# Revit family: 265-91-001 DN700-800
name_source: partatom
category: Pipe Accessories
units: mm (PartAtom-declared; Revit-internal decimal feet)

## family parameters
Always vertical = Yes
Cut with Voids When Loaded = No
Part Type = Valve - Breaks Into
Round Connector Dimension = Use Diameter
Shared = No
Work Plane-Based = No

## types (4) — shared parameters
25 = 25 mm  [stored 0.082021 ft]
Bolt.no = 24 mm  [stored 0.0787402 ft]
DN700_PN10 = 265-9-0700-11-04036401
DN700_PN16 = 265-9-0700-10-14036400
DN800_PN10 = 265-9-0800-11-04036401
DN800_PN16 = 265-9-0800-10-14036400
Description_ = AVK DISMANTLING JOINT WITH CENTRE FLANGE, PN10/16
Raised_dis = 5 mm  [stored 0.0164042 ft]
Search_table = 265-91-001 DN700-800
URL_product_pages = https://www.avkvalves.com
zero-valued in all types: Default Elevation

## per-type parameters (varying)
| type | B1 | Bore | D | DN | FL_T | FL_T/2 | L | L1 | L11 | L2 | L3 | Nut_T | PCD | PN | S | S11 | T | T1 | offset | raised_R |
| DN700_PN16 | 41 mm | 350 mm | 455 mm | 700 mm | 40 mm  [stored 0.131234 ft] | 20 mm  [stored 0.0656168 ft] | 515 mm | 204 mm | 300 mm  [stored 0.984252 ft] | 33 mm  [stored 0.108268 ft] | 20 mm  [stored 0.0656168 ft] | 24 mm  [stored 0.0787402 ft] | 420 mm | 16 mm  [stored 0.0524934 ft] | 33 mm  [stored 0.108268 ft] | 45 mm  [stored 0.147638 ft] | 12 mm  [stored 0.0393701 ft] | 30 mm  [stored 0.0984252 ft] | 12 mm  [stored 0.0393701 ft] | 387 mm |
| DN700_PN10 | 34 mm | 350 mm | 448 mm | 700 mm | 35 mm  [stored 0.114829 ft] | 18 mm  [stored 0.0590551 ft] | 430 mm | 177 mm | 260 mm  [stored 0.853018 ft] | 28 mm  [stored 0.0918635 ft] | 18 mm  [stored 0.0590551 ft] | 21 mm  [stored 0.0688976 ft] | 420 mm | 10 mm  [stored 0.0328084 ft] | 27 mm  [stored 0.0885827 ft] | 36 mm  [stored 0.11811 ft] | 11 mm | 26 mm | 9 mm  [stored 0.0295276 ft] | 380 mm |
| DN800_PN16 | 44 mm | 400 mm | 513 mm | 800 mm | 43 mm  [stored 0.141076 ft] | 22 mm | 545 mm | 218 mm | 320 mm | 35 mm  [stored 0.114829 ft] | 22 mm | 26 mm | 475 mm | 16 mm  [stored 0.0524934 ft] | 36 mm  [stored 0.11811 ft] | 49 mm | 13 mm  [stored 0.0426509 ft] | 32 mm  [stored 0.104987 ft] | 13 mm  [stored 0.0426509 ft] | 436 mm |
| DN800_PN10 | 38 mm | 400 mm | 508 mm | 800 mm | 38 mm | 19 mm  [stored 0.062336 ft] | 480 mm | 197 mm | 290 mm  [stored 0.951444 ft] | 31 mm | 19 mm  [stored 0.062336 ft] | 23 mm | 475 mm | 10 mm  [stored 0.0328084 ft] | 30 mm  [stored 0.0984252 ft] | 41 mm | 11 mm | 28 mm  [stored 0.0918635 ft] | 11 mm | 431 mm |

note: [stored X ft] marks values corroborated as IEEE doubles in the binary element streams (Revit-internal decimal feet)

## geometry (parser evidence)
native form markers: Sweep x11
no freeform markers — native parametric forms only
